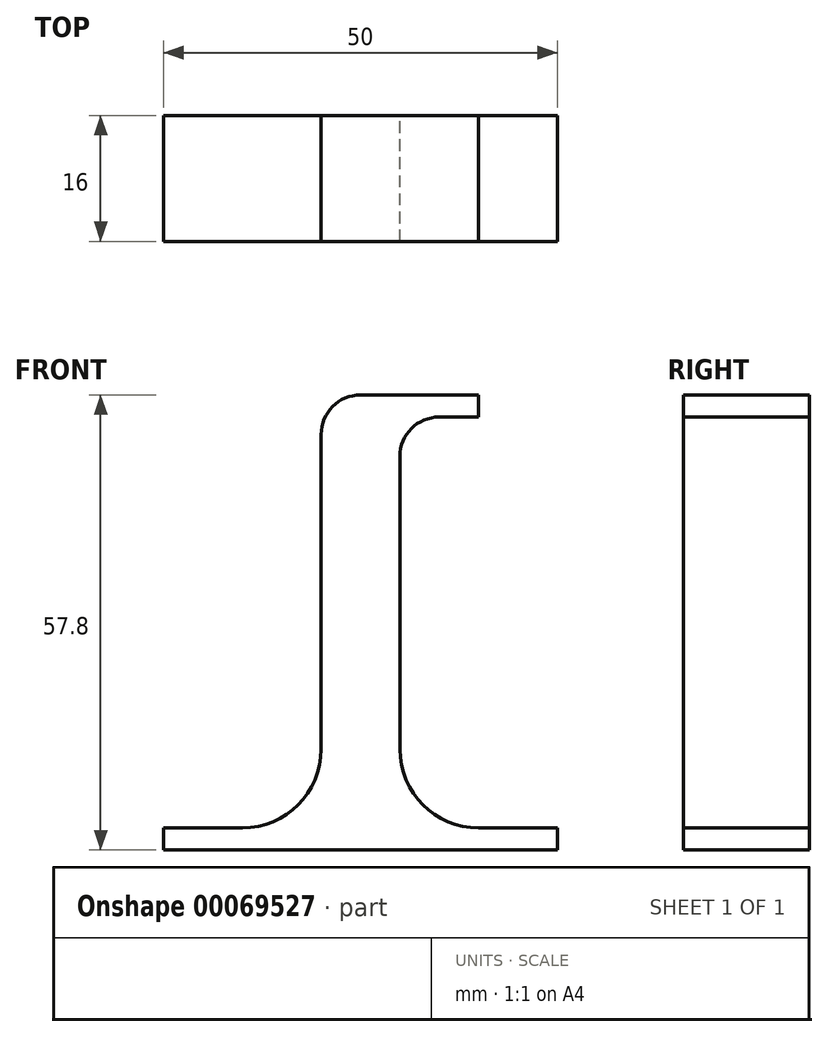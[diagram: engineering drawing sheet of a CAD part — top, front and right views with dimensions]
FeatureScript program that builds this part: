
annotation { "Feature Type Name" : "Feature", "Feature Type Description" : "" }
export const myFeature = defineFeature(function(context is Context, id is Id, definition is map)
    precondition{}
    {
        {
            var Q0;
            Q0=qCreatedBy(makeId("Front.planeOp"),FACE);
            var sketch = newSketch(context, id + "F0", { "sketchPlane" : qUnion([Q0])});
            skLineSegment(sketch, "E0", {"start": v(0, 0) * mm, "end": v(0, 55) * mm});
            skLineSegment(sketch, "E1", {"start": v(0, 55) * mm, "end": v(10, 55) * mm});
            skLineSegment(sketch, "E2", {"start": v(10, 55) * mm, "end": v(10, 57.8) * mm});
            skLineSegment(sketch, "E3", {"start": v(10, 57.8) * mm, "end": v(-10, 57.8) * mm});
            skLineSegment(sketch, "E4", {"start": v(-10, 57.8) * mm, "end": v(-10, 2.8) * mm});
            skLineSegment(sketch, "E5", {"start": v(-10, 2.8) * mm, "end": v(0, 2.8) * mm});
            skLineSegment(sketch, "E6", {"start": v(20, 0) * mm, "end": v(-30, 0) * mm});
            skLineSegment(sketch, "E7", {"start": v(-30, 0) * mm, "end": v(-30, 2.8) * mm});
            skLineSegment(sketch, "E8", {"start": v(-30, 2.8) * mm, "end": v(-10, 2.8) * mm});
            skLineSegment(sketch, "E9", {"start": v(0, 2.8) * mm, "end": v(20, 2.8) * mm});
            skLineSegment(sketch, "E10", {"start": v(20, 2.8) * mm, "end": v(20, 0) * mm});
            skSolve(sketch);
        }
        {
            var Q0;
            {var subQ4=sQuery(id+"F0.wireOp",EDGE,"E5");Q0=makeQuery(id+"F0.imprint","IMPRINT",FACE,{"disambiguationData":[TD([[makeQuery(id+"F0.imprint","IMPRINT",EDGE,{"derivedFrom":subQ4}),-1.0]])]});}
            var Q1;
            {var subQ0=sQuery(id+"F0.wireOp",EDGE,"E9");Q1=makeQuery(id+"F0.imprint","IMPRINT",FACE,{"disambiguationData":[TD([[makeQuery(id+"F0.imprint","IMPRINT",EDGE,{"derivedFrom":subQ0}),-1.0]])]});}
            var Q2;
            {var subQ0=sQuery(id+"F0.wireOp",EDGE,"E1");Q2=makeQuery(id+"F0.imprint","IMPRINT",FACE,{"disambiguationData":[TD([[makeQuery(id+"F0.imprint","IMPRINT",EDGE,{"derivedFrom":subQ0}),1.0]])]});}
            extrude(context, id + "F1", {"entities" : qUnion([Q0, Q1, Q2]), "depth" : 16 * mm, "offsetDistance" : 25 * mm});
        }
        {
            var Q0;
            Q0=makeQuery(id+"F1.opExtrude","SWEPT_EDGE",EDGE,{"disambiguationData":[OSD([sQuery(id+"F0.wireOp",EDGE,"E4"),sQuery(id+"F0.wireOp",EDGE,"E5"),sQuery(id+"F0.wireOp",EDGE,"E8")])]});
            var Q1;
            Q1=makeQuery(id+"F1.opExtrude","SWEPT_EDGE",EDGE,{"disambiguationData":[OSD([sQuery(id+"F0.wireOp",EDGE,"E0"),sQuery(id+"F0.wireOp",EDGE,"E5"),sQuery(id+"F0.wireOp",EDGE,"E9")])]});
            fillet(context, id + "F2", {"entities" : qUnion([Q0, Q1]), "tangentPropagation" : true, "radius" : 10 * mm, "defaultsChanged" : false, "vertexSettings" : [], "allowEdgeOverflow" : false});
        }
        {
            var Q0;
            Q0=makeQuery(id+"F1.opExtrude","SWEPT_EDGE",EDGE,{"disambiguationData":[OSD([sQuery(id+"F0.wireOp",EDGE,"E3"),sQuery(id+"F0.wireOp",EDGE,"E4")])]});
            var Q1;
            Q1=makeQuery(id+"F1.opExtrude","SWEPT_EDGE",EDGE,{"disambiguationData":[OSD([sQuery(id+"F0.wireOp",EDGE,"E0"),sQuery(id+"F0.wireOp",EDGE,"E1")])]});
            fillet(context, id + "F3", {"entities" : qUnion([Q0, Q1]), "tangentPropagation" : true, "radius" : 5 * mm, "defaultsChanged" : false, "vertexSettings" : [], "allowEdgeOverflow" : false});
        }
    });
